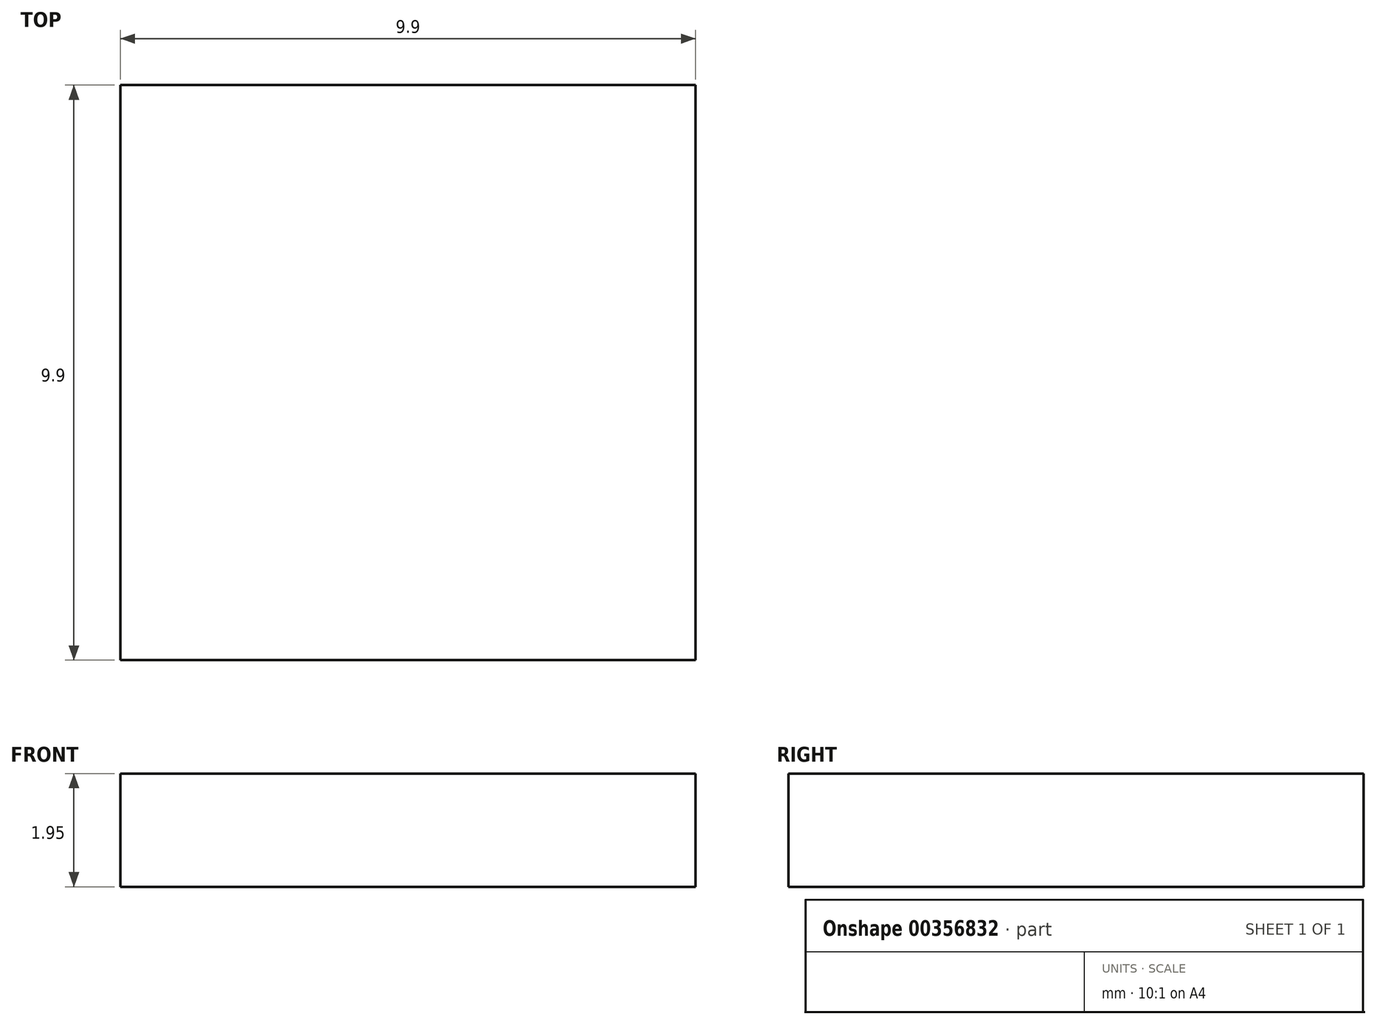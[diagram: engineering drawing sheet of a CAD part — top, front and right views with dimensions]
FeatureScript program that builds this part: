
annotation { "Feature Type Name" : "Feature", "Feature Type Description" : "" }
export const myFeature = defineFeature(function(context is Context, id is Id, definition is map)
    precondition{}
    {
        {
            var Q0;
            Q0=qCreatedBy(makeId("Top.planeOp"),FACE);
            var sketch = newSketch(context, id + "F0", { "sketchPlane" : qUnion([Q0])});
            skLineSegment(sketch, "E0.bottom", {"start": v(0, 0) * mm, "end": v(9.9, 0) * mm});
            skLineSegment(sketch, "E0.top", {"start": v(0, -9.9) * mm, "end": v(9.9, -9.9) * mm});
            skLineSegment(sketch, "E0.left", {"start": v(0, 0) * mm, "end": v(0, -9.9) * mm});
            skLineSegment(sketch, "E0.right", {"start": v(9.9, 0) * mm, "end": v(9.9, -9.9) * mm});
            skSolve(sketch);
        }
        {
            var Q0;
            Q0 = qSketchRegion(id + "F0", true);
            extrude(context, id + "F1", {"entities" : qUnion([Q0]), "depth" : (0.13 * 15) * mm, "offsetDistance" : 25 * mm});
        }
    });
